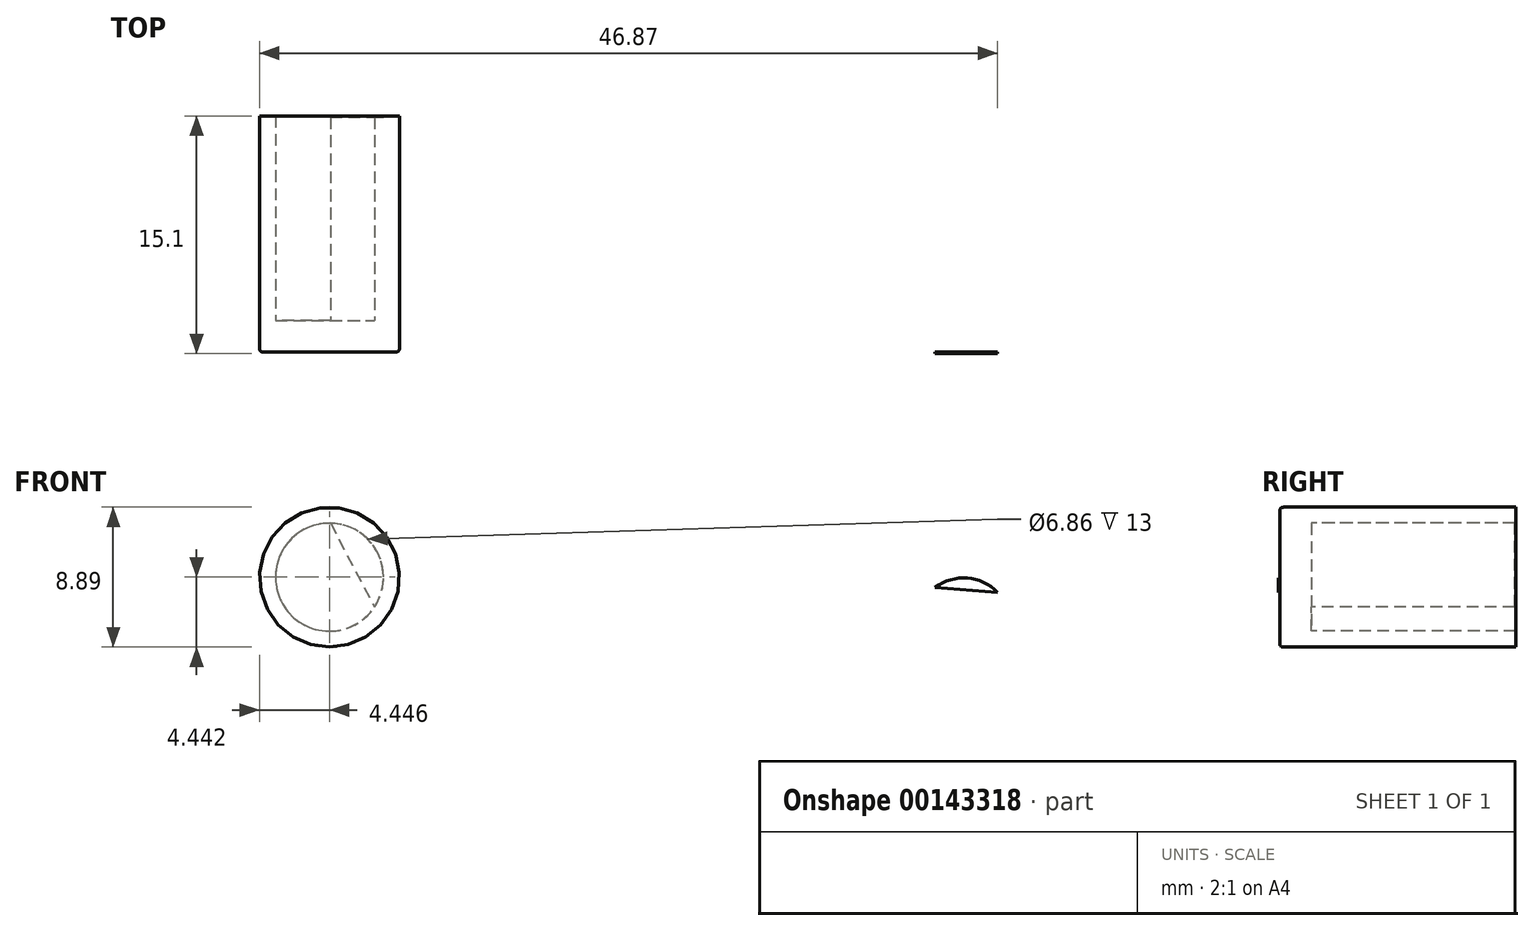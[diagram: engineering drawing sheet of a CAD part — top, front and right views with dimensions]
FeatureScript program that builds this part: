
annotation { "Feature Type Name" : "Feature", "Feature Type Description" : "" }
export const myFeature = defineFeature(function(context is Context, id is Id, definition is map)
    precondition{}
    {
        {
            var Q0;
            Q0=qCreatedBy(makeId("Front.planeOp"),FACE);
            var sketch = newSketch(context, id + "F0", { "sketchPlane" : qUnion([Q0])});
            skCircle(sketch, "E0", {"center": v(-59.22, 37.21) * mm, "radius": 3.43 * mm});
            skCircle(sketch, "E1", {"center": v(-59.22, 37.21) * mm, "radius": 4.45 * mm});
            skLineSegment(sketch, "E2", {"start": v(-59.17, 40.64) * mm, "end": v(-56.36, 35.32) * mm});
            skSolve(sketch);
        }
        {
            var Q0;
            Q0 = qSketchRegion(id + "F0", true);
            extrude(context, id + "F1", {"entities" : qUnion([Q0]), "oppositeDirection" : true, "depth" : 15 * mm});
        }
        {
            var Q0;
            {var subQ0=sQuery(id+"F0.wireOp",EDGE,"E2");Q0=makeQuery(id+"F0.imprint","IMPRINT",FACE,{"disambiguationData":[TD([[makeQuery(id+"F0.imprint","IMPRINT",EDGE,{"derivedFrom":subQ0}),-1.0]])]});}
            extrude(context, id + "F2", {"entities" : qUnion([Q0]), "operationType" : NewBodyOperationType.ADD, "oppositeDirection" : true, "depth" : 2 * mm});
        }
        {
            var Q0;
            Q0=qCreatedBy(makeId("Front.planeOp"),FACE);
            var sketch = newSketch(context, id + "F3", { "sketchPlane" : qUnion([Q0])});
            skArc(sketch, "E3", {"start": v(-16.8, 36.25) * mm, "mid": v(-18.71, 37.16) * mm, "end": v(-20.75, 36.56) * mm});
            skLineSegment(sketch, "E4", {"start": v(-16.8, 36.25) * mm, "end": v(-20.75, 36.56) * mm});
            skSolve(sketch);
        }
        {
            var Q0;
            Q0 = qSketchRegion(id + "F3", true);
            extrude(context, id + "F4", {"entities" : qUnion([Q0]), "depth" : 0.1 * mm});
        }
        {
            var Q0;
            {var subQ0=sQuery(id+"F0.wireOp",EDGE,"E2");Q0=makeQuery(id+"F0.imprint","IMPRINT",FACE,{"disambiguationData":[TD([[makeQuery(id+"F0.imprint","IMPRINT",EDGE,{"derivedFrom":subQ0}),1.0]])]});}
            extrude(context, id + "F5", {"entities" : qUnion([Q0]), "operationType" : NewBodyOperationType.ADD, "oppositeDirection" : true, "depth" : 14.92 * mm});
        }
        {
            var Q0;
            Q0=makeQuery(id+"F1.opExtrude","CAP_EDGE",EDGE,{"disambiguationData":[OSD([sQuery(id+"F0.wireOp",EDGE,"E1")])],"isStart":true});
            fillet(context, id + "F6", {"entities" : qUnion([Q0]), "radius" : 0.25 * mm, "rho" : 0.5, "crossSection" : FilletCrossSection.CONIC, "allowEdgeOverflow" : false});
        }
    });
